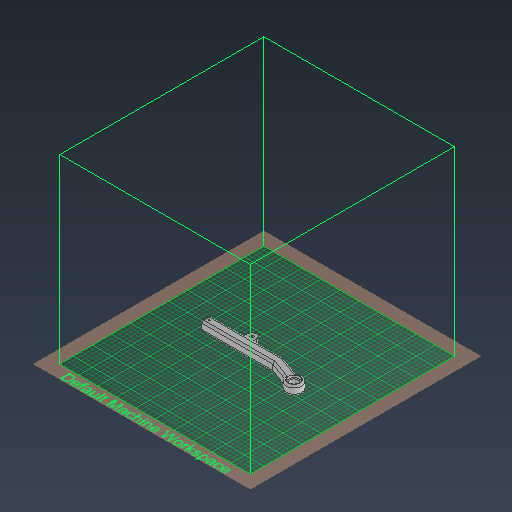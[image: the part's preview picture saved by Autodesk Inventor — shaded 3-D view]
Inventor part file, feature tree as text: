
AUTODESK INVENTOR PART (.ipt)
format: ipt  version: 2021 (Build 250183000, 183)  size: 557,568 bytes
history: native  units: mm
features: extrude x11, sketch x9, fillet x2, shell x1
ambient origin geometry x8: Origin, YZ Plane, XZ Plane, XY Plane, X Axis, Y Axis, Z Axis, Center Point
bodies: Volumenkörper1 (feature_tree)
feature tree (23):
  sketch  "Skizze1"  dims[d5=20.0mm d56=0.0mm]
  sketch  "Skizze4"  dims[d57=0.0mm d58=60.0mm]
  extrude  "Extrusion1"  TaperAngle=0.0deg  [1 undecoded]
  sketch  "Skizze13"  dims[d129=12.0mm d130=0.0mm d133=3.2mm]
  extrude  "Extrusion13"  Depth=60.0mm
  extrude  "Extrusion14"  Depth=10.0mm TaperAngle=0.0deg
  shell  "Wandung2"  Thickness=10.0mm
  extrude  "Extrusion11"  Depth=12.0mm
  extrude  "Extrusion12"  Depth=10.0mm TaperAngle=0.0deg
  extrude  "Extrusion15"  Depth=3.490659mm
  extrude  "Extrusion16"  Depth=10.0mm
  extrude  "Extrusion17"  Depth=10.0mm
  extrude  "Extrusion18"  Depth=2.0mm
  fillet  "Rundung7"  Radius=34.0mm
  extrude  "Extrusion19"  Depth=2.0mm TaperAngle=0.0deg
  extrude  "Extrusion20"  Depth=2.0mm TaperAngle=0.0deg
  fillet  "Rundung8"  Radius=2.6mm
  sketch  "Skizze12"  dims[d74=20.0mm d75=20.0mm d78=10.0mm d79=20.0mm d80=0.0mm d116=10.0mm]
  sketch  "Skizze14"  dims[d135=6.0mm d136=10.0mm d137=0.0mm]
  sketch  "Skizze15"  dims[d138=160.0mm d140=3.490659mm]
  sketch  "Skizze16"  dims[d141=10.0mm d142=110.0mm]
  sketch  "Skizze17"  dims[d143=50.0mm d144=10.0mm]
  sketch  "Skizze18"  dims[d147=10.0mm d148=24.3mm d149=34.0mm d150=20.0mm d151=0.0mm d152=20.0mm d153=0.0mm d154=2.6mm d155=4.0mm d157=18.0mm d158=10.0mm d159=0.0mm d160=10.0mm d161=10.0mm d162=20.0mm d163=6.0mm d164=0.0mm d165=7.0mm d166=10.0mm d167=10.0mm d168=10.0mm d169=3.0mm d170=0.0mm d171=3.2mm d172=10.0mm d173=10.0mm d174=3.0mm d175=0.0mm d176=12.0mm d177=12.0mm d178=6.0mm d179=12.0mm d180=12.0mm d181=6.0mm d182=3.0mm d183=0.0mm d184=12.0mm d185=12.0mm d186=6.0mm d187=3.0mm d188=0.0mm d189=2.0mm d81=0.5mm d82=0.872665mm d83=0.5mm d84=0.872665mm]
note: 1 required parameter value undecoded (feature->parameter linkage not recoverable at this tier; creation-order binding heuristic only, values carry confidence <= 0.55)
